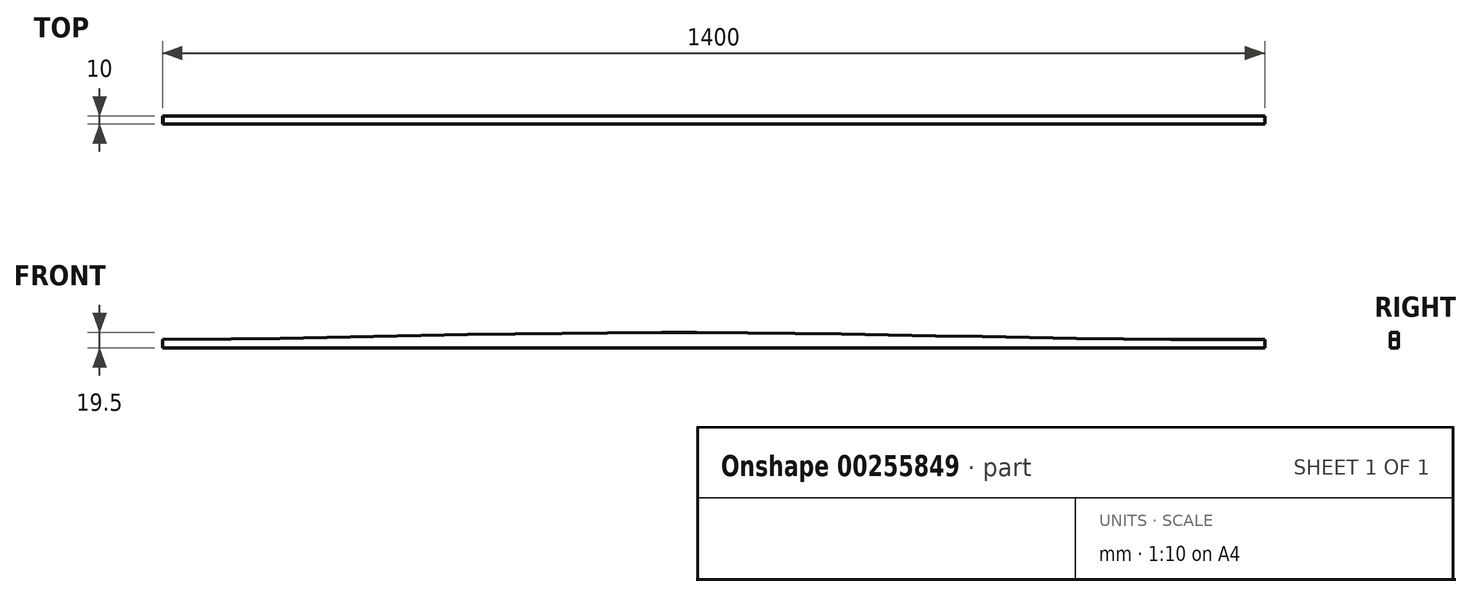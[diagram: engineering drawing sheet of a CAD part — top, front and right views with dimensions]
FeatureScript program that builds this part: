
annotation { "Feature Type Name" : "Feature", "Feature Type Description" : "" }
export const myFeature = defineFeature(function(context is Context, id is Id, definition is map)
    precondition{}
    {
        {
            var Q0;
            Q0=qCreatedBy(makeId("Front.planeOp"),FACE);
            var sketch = newSketch(context, id + "F0", { "sketchPlane" : qUnion([Q0])});
            skLineSegment(sketch, "E0", {"start": v(-6.9, 13.66) * mm, "end": v(-6.9, 3.16) * mm});
            skLineSegment(sketch, "E1", {"start": v(-6.9, 3.16) * mm, "end": v(1393.1, 3.16) * mm});
            skPoint(sketch, "E2", {"position": v(-5.9, 3.16) * mm});
            skPoint(sketch, "E3", {"position": v(93.1, 3.16) * mm});
            skPoint(sketch, "E4", {"position": v(143.1, 3.16) * mm});
            skPoint(sketch, "E5", {"position": v(243.1, 3.16) * mm});
            skPoint(sketch, "E6", {"position": v(193.1, 3.16) * mm});
            skPoint(sketch, "E7", {"position": v(293.1, 3.16) * mm});
            skPoint(sketch, "E8", {"position": v(343.1, 3.16) * mm});
            skPoint(sketch, "E9", {"position": v(393.1, 3.16) * mm});
            skPoint(sketch, "E10", {"position": v(443.1, 3.16) * mm});
            skPoint(sketch, "E11", {"position": v(493.1, 3.16) * mm});
            skPoint(sketch, "E12", {"position": v(543.1, 3.16) * mm});
            skPoint(sketch, "E13", {"position": v(593.1, 3.16) * mm});
            skPoint(sketch, "E14", {"position": v(643.1, 3.16) * mm});
            skPoint(sketch, "E15", {"position": v(693.1, 3.16) * mm});
            skPoint(sketch, "E16", {"position": v(743.1, 3.16) * mm});
            skPoint(sketch, "E17", {"position": v(793.1, 3.16) * mm});
            skPoint(sketch, "E18", {"position": v(843.1, 3.16) * mm});
            skPoint(sketch, "E19", {"position": v(893.1, 3.16) * mm});
            skPoint(sketch, "E20", {"position": v(943.1, 3.16) * mm});
            skPoint(sketch, "E21", {"position": v(993.1, 3.16) * mm});
            skPoint(sketch, "E22", {"position": v(1043.1, 3.16) * mm});
            skPoint(sketch, "E23", {"position": v(1093.1, 3.16) * mm});
            skPoint(sketch, "E24", {"position": v(1143.1, 3.16) * mm});
            skPoint(sketch, "E25", {"position": v(1193.1, 3.16) * mm});
            skPoint(sketch, "E26", {"position": v(1243.1, 3.16) * mm});
            skPoint(sketch, "E27", {"position": v(1293.1, 3.16) * mm});
            skPoint(sketch, "E28", {"position": v(1293.4, 3.16) * mm});
            skPoint(sketch, "E29", {"position": v(1343.4, 3.16) * mm});
            skLineSegment(sketch, "E30", {"start": v(-6.9, 13.66) * mm, "end": v(-5.9, 14.1) * mm});
            skFitSpline(sketch, "E31", {"points": [v(-5.9, 14.1) * mm, v(93.1, 14.64) * mm, v(143.1, 15.35) * mm, v(193.1, 16.2) * mm, v(243.1, 17.16) * mm, v(293.1, 18.16) * mm, v(343.1, 19.16) * mm, v(393.1, 20.11) * mm, v(443.1, 20.96) * mm, v(493.1, 21.68) * mm, v(543.1, 22.21) * mm, v(593.1, 22.55) * mm, v(642.96, 22.66) * mm, v(643.1, 22.66) * mm, v(693.1, 22.55) * mm, v(743.1, 22.22) * mm, v(793.1, 21.69) * mm, v(843.1, 20.97) * mm, v(893.1, 20.12) * mm, v(943.1, 19.17) * mm, v(993.1, 18.17) * mm, v(1043.1, 17.17) * mm, v(1093.1, 16.22) * mm, v(1143.1, 15.37) * mm, v(1193.1, 14.65) * mm, v(1243.1, 14.11) * mm, v(1293.4, 13.78) * mm, v(1343.4, 13.66) * mm, v(1393.1, 13.66) * mm], "startDerivative": vector(2101.04, 7.9) * mm, "endDerivative": vector(1365.64, 0.5) * mm});
            skLineSegment(sketch, "E32", {"start": v(1393.1, 13.66) * mm, "end": v(1393.1, 3.16) * mm});
            skSolve(sketch);
        }
        {
            var Q0;
            Q0=makeQuery(id+"F0.imprint","IMPRINT",FACE,{"disambiguationData":[TD([[makeQuery(id+"F0.imprint","IMPRINT",EDGE,{"derivedFrom":sQuery(id+"F0.wireOp",EDGE,"E0")}),1.0]])]});
            extrude(context, id + "F1", {"entities" : qUnion([Q0]), "depth" : 10 * mm});
        }
    });
